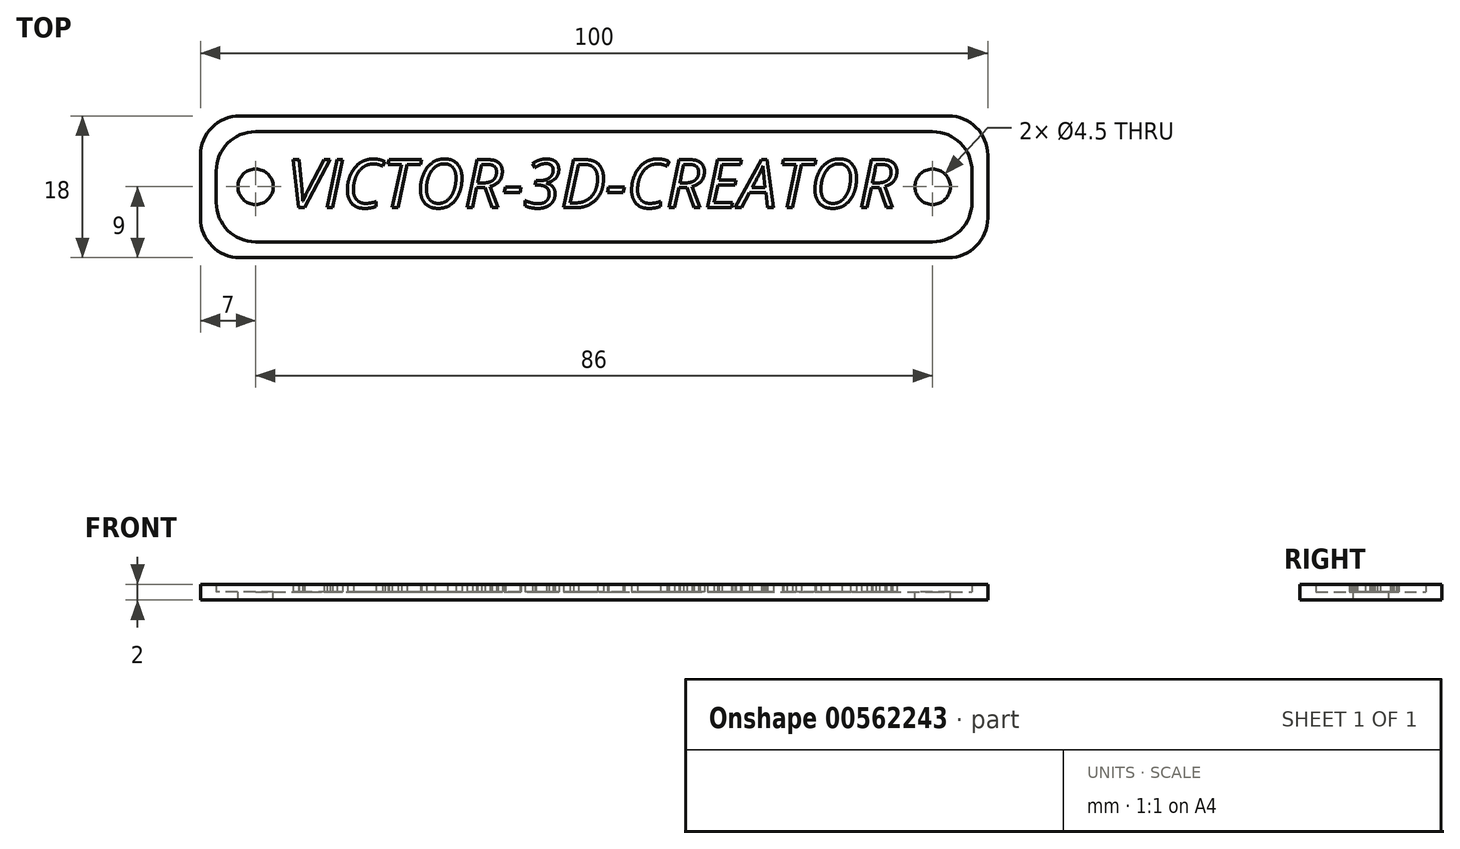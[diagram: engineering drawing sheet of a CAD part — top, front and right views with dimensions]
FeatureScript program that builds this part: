
annotation { "Feature Type Name" : "Feature", "Feature Type Description" : "" }
export const myFeature = defineFeature(function(context is Context, id is Id, definition is map)
    precondition{}
    {
        {
            var Q0;
            Q0=qCreatedBy(makeId("Top.planeOp"),FACE);
            var sketch = newSketch(context, id + "F0", { "sketchPlane" : qUnion([Q0])});
            skLineSegment(sketch, "E0.bottom", {"start": v(0, 0) * mm, "end": v(100, 0) * mm});
            skLineSegment(sketch, "E0.top", {"start": v(0, 18) * mm, "end": v(100, 18) * mm});
            skLineSegment(sketch, "E0.left", {"start": v(0, 0) * mm, "end": v(0, 18) * mm});
            skLineSegment(sketch, "E0.right", {"start": v(100, 0) * mm, "end": v(100, 18) * mm});
            skCircle(sketch, "E1", {"center": v(7, 9) * mm, "radius": 2.25 * mm});
            skCircle(sketch, "E2", {"center": v(93, 9) * mm, "radius": 2.25 * mm});
            skSolve(sketch);
        }
        {
            var Q0;
            Q0=qSketchRegion(id+"F0",true);
            var Q1;
            Q1 = qSketchRegion(id + "F2", true);
            extrude(context, id + "F1", {"entities" : qUnion([Q0, Q1]), "oppositeDirection" : true, "depth" : 1 * mm, "offsetDistance" : 25 * mm});
        }
        {
            var Q0;
            Q0=makeQuery(id+"F1.opExtrude","CAP_FACE",FACE,{"disambiguationData":[OSD([sQuery(id+"F0.wireOp",EDGE,"E0.bottom"),sQuery(id+"F0.wireOp",EDGE,"E0.top"),sQuery(id+"F0.wireOp",EDGE,"E0.left"),sQuery(id+"F0.wireOp",EDGE,"E0.right"),sQuery(id+"F0.wireOp",EDGE,"E1"),sQuery(id+"F0.wireOp",EDGE,"E2")])],"isStart":true});
            var sketch = newSketch(context, id + "F2", { "sketchPlane" : qUnion([Q0])});
            skText(sketch, "E3", { "text": "VICTOR-3D-CREATOR", "fontName": "OpenSans-Italic.ttf"});
            const initialGuessF2  = {"E3": [0.011, 0.00633, 1, 0, 0.00617]};
            skSetInitialGuess(sketch, initialGuessF2);
            skSolve(sketch);
        }
        {
            var Q0;
            Q0=qSketchRegion(id+"F2",true);
            extrude(context, id + "F3", {"entities" : qUnion([Q0]), "operationType" : NewBodyOperationType.ADD, "depth" : 1 * mm, "offsetDistance" : 25 * mm});
        }
        {
            var Q0;
            {var subQ0=sQuery(id+"F0.wireOp",EDGE,"E0.top");var subQ118=sQuery(id+"F0.wireOp",EDGE,"E0.right");var subQ127=sQuery(id+"F0.wireOp",EDGE,"E0.bottom");var subQ128=makeQuery(id+"F1.opExtrude","SWEPT_FACE",FACE,{"disambiguationData":[OSD([subQ127])]});var subQ129=sQuery(id+"F0.wireOp",EDGE,"E1");var subQ139=sQuery(id+"F0.wireOp",EDGE,"E2");var subQ143=sQuery(id+"F0.wireOp",EDGE,"E0.left");Q0=makeQuery(id+"FFJBjQclBaa1cPK_1.boolean.opBoolean","SPLIT",FACE,{"disambiguationData":[TD([subQ128])],"derivedFrom":makeQuery(id+"F3.boolean.opBoolean","SPLIT",FACE,{"disambiguationData":[TD([subQ128])],"derivedFrom":makeQuery(id+"F1.opExtrude","CAP_FACE",FACE,{"disambiguationData":[OSD([subQ127,subQ0,subQ143,subQ118,subQ129,subQ139])],"isStart":true})})});}
            var sketch = newSketch(context, id + "F4", { "sketchPlane" : qUnion([Q0])});
            skLineSegment(sketch, "E4.bottom", {"start": v(2, 16) * mm, "end": v(98, 16) * mm});
            skLineSegment(sketch, "E4.top", {"start": v(2, 2) * mm, "end": v(98, 2) * mm});
            skLineSegment(sketch, "E4.left", {"start": v(2, 16) * mm, "end": v(2, 2) * mm});
            skLineSegment(sketch, "E4.right", {"start": v(98, 16) * mm, "end": v(98, 2) * mm});
            skSolve(sketch);
        }
        {
            var Q0;
            Q0=makeQuery(id+"F4.imprint","IMPRINT",FACE,{"disambiguationData":[TD([[makeQuery(id+"F4.imprint","IMPRINT",EDGE,{"derivedFrom":sQuery(id+"F4.wireOp",EDGE,"E4.bottom")}),1.0]])]});
            extrude(context, id + "F5", {"entities" : qUnion([Q0]), "operationType" : NewBodyOperationType.ADD, "depth" : 1 * mm, "offsetDistance" : 25 * mm});
        }
        {
            var Q0;
            {var subQ0=sQuery(id+"F0.wireOp",EDGE,"E0.left");var subQ1=sQuery(id+"F0.wireOp",EDGE,"E0.top");Q0=makeQuery(id+"F5.boolean.opBoolean","MERGE",EDGE,{"derivedFrom":[makeQuery(id+"F1.opExtrude","SWEPT_EDGE",EDGE,{"disambiguationData":[OSD([subQ1,subQ0])]}),makeQuery(id+"F5.opExtrude","SWEPT_EDGE",EDGE,{"disambiguationData":[OSD([subQ1,subQ0])]})]});}
            var Q1;
            {var subQ0=sQuery(id+"F0.wireOp",EDGE,"E0.left");var subQ1=sQuery(id+"F0.wireOp",EDGE,"E0.bottom");Q1=makeQuery(id+"F5.boolean.opBoolean","MERGE",EDGE,{"derivedFrom":[makeQuery(id+"F1.opExtrude","SWEPT_EDGE",EDGE,{"disambiguationData":[OSD([subQ1,subQ0])]}),makeQuery(id+"F5.opExtrude","SWEPT_EDGE",EDGE,{"disambiguationData":[OSD([subQ1,subQ0])]})]});}
            var Q2;
            {var subQ0=sQuery(id+"F0.wireOp",EDGE,"E0.right");var subQ1=sQuery(id+"F0.wireOp",EDGE,"E0.top");Q2=makeQuery(id+"F5.boolean.opBoolean","MERGE",EDGE,{"derivedFrom":[makeQuery(id+"F1.opExtrude","SWEPT_EDGE",EDGE,{"disambiguationData":[OSD([subQ1,subQ0])]}),makeQuery(id+"F5.opExtrude","SWEPT_EDGE",EDGE,{"disambiguationData":[OSD([subQ1,subQ0])]})]});}
            var Q3;
            {var subQ0=sQuery(id+"F0.wireOp",EDGE,"E0.right");var subQ1=sQuery(id+"F0.wireOp",EDGE,"E0.bottom");Q3=makeQuery(id+"F5.boolean.opBoolean","MERGE",EDGE,{"derivedFrom":[makeQuery(id+"F1.opExtrude","SWEPT_EDGE",EDGE,{"disambiguationData":[OSD([subQ1,subQ0])]}),makeQuery(id+"F5.opExtrude","SWEPT_EDGE",EDGE,{"disambiguationData":[OSD([subQ1,subQ0])]})]});}
            var Q4;
            Q4=makeQuery(id+"F5.opExtrude","SWEPT_EDGE",EDGE,{"disambiguationData":[OSD([sQuery(id+"F4.wireOp",EDGE,"E4.bottom"),sQuery(id+"F4.wireOp",EDGE,"E4.left")])]});
            var Q5;
            Q5=makeQuery(id+"F5.opExtrude","SWEPT_EDGE",EDGE,{"disambiguationData":[OSD([sQuery(id+"F4.wireOp",EDGE,"E4.top"),sQuery(id+"F4.wireOp",EDGE,"E4.left")])]});
            var Q6;
            Q6=makeQuery(id+"F5.opExtrude","SWEPT_EDGE",EDGE,{"disambiguationData":[OSD([sQuery(id+"F4.wireOp",EDGE,"E4.bottom"),sQuery(id+"F4.wireOp",EDGE,"E4.right")])]});
            var Q7;
            Q7=makeQuery(id+"F5.opExtrude","SWEPT_EDGE",EDGE,{"disambiguationData":[OSD([sQuery(id+"F4.wireOp",EDGE,"E4.top"),sQuery(id+"F4.wireOp",EDGE,"E4.right")])]});
            fillet(context, id + "F6", {"entities" : qUnion([Q0, Q1, Q2, Q3, Q4, Q5, Q6, Q7]), "radius" : 5 * mm, "tangentPropagation" : true, "allowEdgeOverflow" : false});
        }
    });
